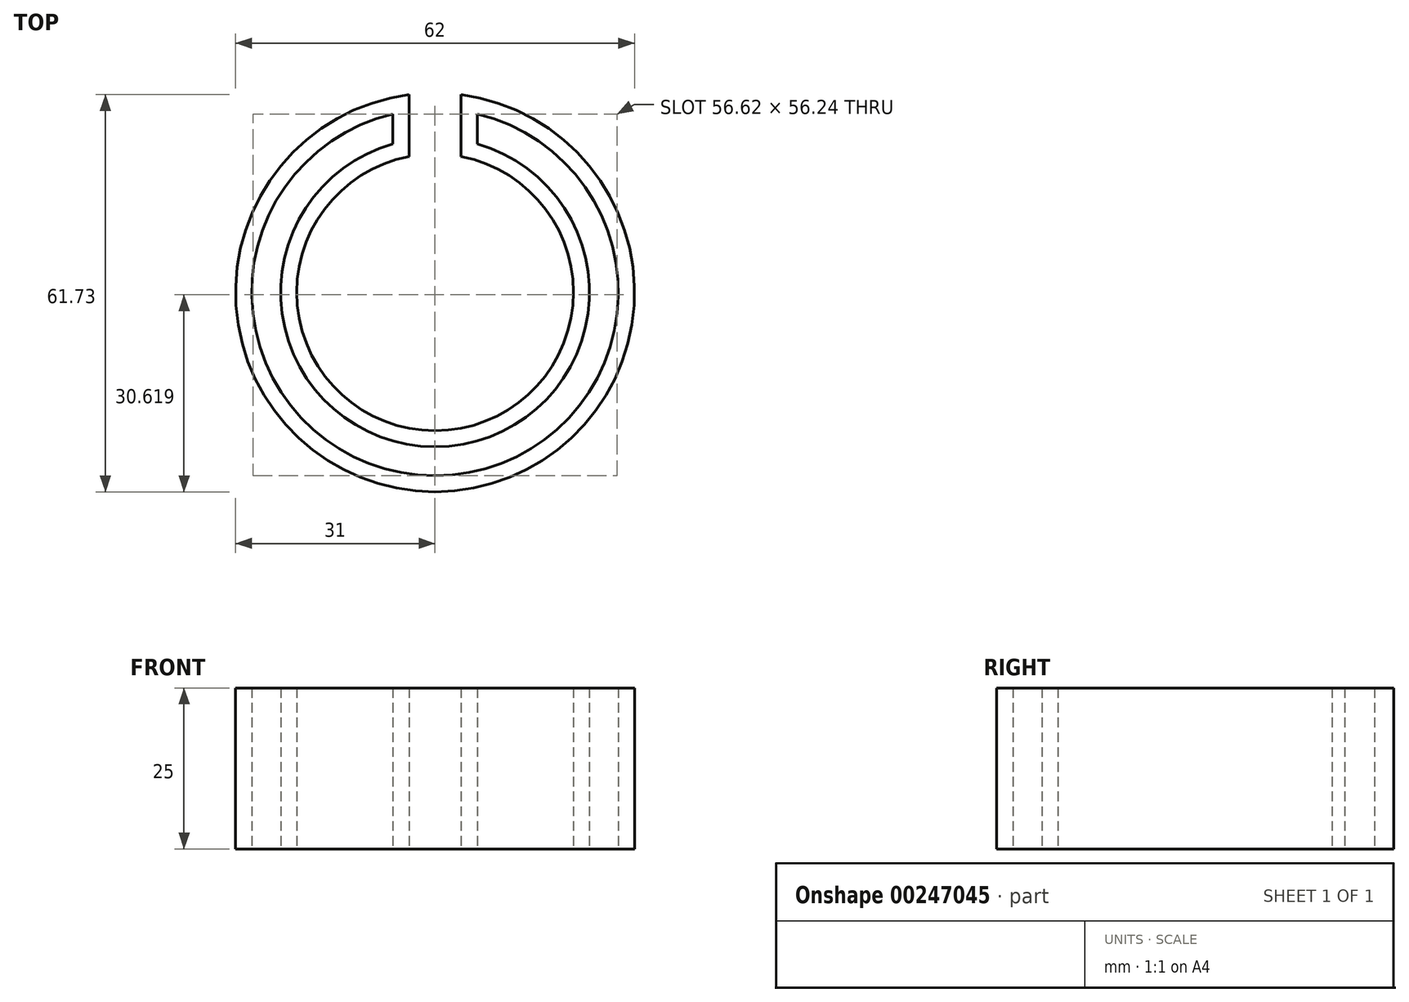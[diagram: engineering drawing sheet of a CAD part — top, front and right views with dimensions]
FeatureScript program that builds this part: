
annotation { "Feature Type Name" : "Feature", "Feature Type Description" : "" }
export const myFeature = defineFeature(function(context is Context, id is Id, definition is map)
    precondition{}
    {
        {
            var Q0;
            Q0=qCreatedBy(makeId("Top.planeOp"),FACE);
            var sketch = newSketch(context, id + "F0", { "sketchPlane" : qUnion([Q0])});
            skCircle(sketch, "E0", {"center": v(0, 0) * mm, "radius": 21.5 * mm});
            skCircle(sketch, "E1", {"center": v(0, 0) * mm, "radius": 31 * mm});
            skSolve(sketch);
        }
        {
            var Q0;
            Q0 = qSketchRegion(id + "F0", true);
            extrude(context, id + "F1", {"entities" : qUnion([Q0]), "depth" : 25 * mm});
        }
        {
            var Q0;
            Q0=makeQuery(id+"F1.opExtrude","CAP_FACE",FACE,{"disambiguationData":[OSD([sQuery(id+"F0.wireOp",EDGE,"E0"),sQuery(id+"F0.wireOp",EDGE,"E1")])],"isStart":false});
            var sketch = newSketch(context, id + "F2", { "sketchPlane" : qUnion([Q0])});
            skLineSegment(sketch, "E2.bottom", {"start": v(-4.05, 32.88) * mm, "end": v(4.05, 32.88) * mm});
            skLineSegment(sketch, "E2.top", {"start": v(-4.05, 17.71) * mm, "end": v(4.05, 17.71) * mm});
            skLineSegment(sketch, "E2.left", {"start": v(-4.05, 32.88) * mm, "end": v(-4.05, 17.71) * mm});
            skLineSegment(sketch, "E2.right", {"start": v(4.05, 32.88) * mm, "end": v(4.05, 17.71) * mm});
            skSolve(sketch);
        }
        {
            var Q0;
            Q0 = qSketchRegion(id + "F2", true);
            extrude(context, id + "F3", {"entities" : qUnion([Q0]), "operationType" : NewBodyOperationType.REMOVE, "oppositeDirection" : true, "depth" : 25 * mm});
        }
        {
            var Q0;
            Q0=makeQuery(id+"F1.opExtrude","CAP_FACE",FACE,{"disambiguationData":[OSD([sQuery(id+"F0.wireOp",EDGE,"E0"),sQuery(id+"F0.wireOp",EDGE,"E1")])],"isStart":true});
            var Q1;
            Q1=makeQuery(id+"F1.opExtrude","CAP_FACE",FACE,{"disambiguationData":[OSD([sQuery(id+"F0.wireOp",EDGE,"E0"),sQuery(id+"F0.wireOp",EDGE,"E1")])],"isStart":false});
            shell(context, id + "F4", {"entities" : qUnion([Q0, Q1]), "thickness" : 2.5 * mm});
        }
    });
